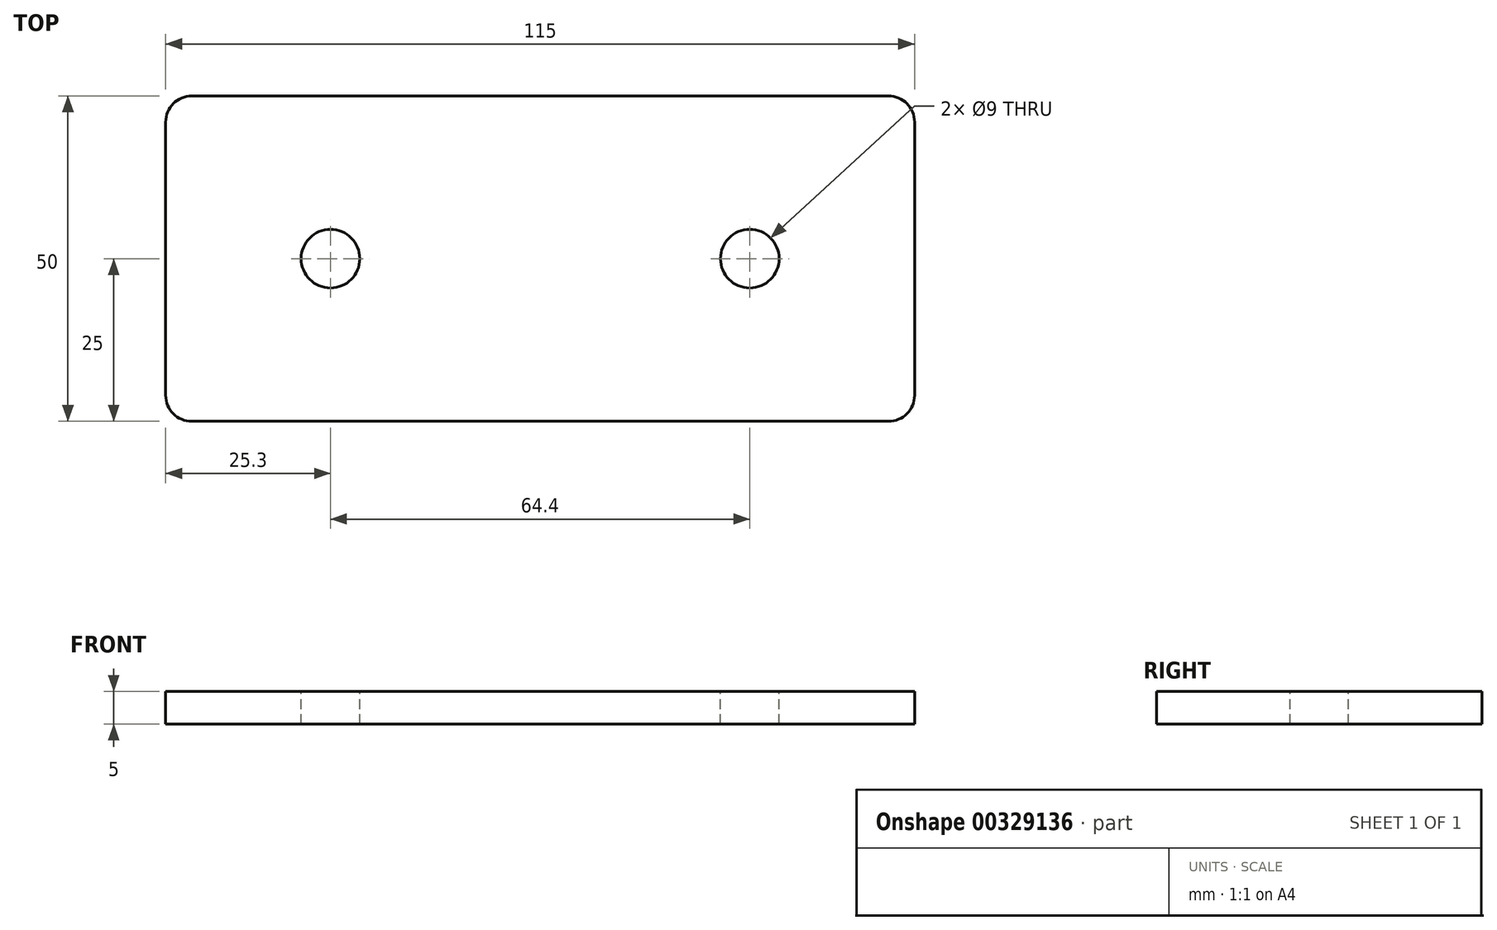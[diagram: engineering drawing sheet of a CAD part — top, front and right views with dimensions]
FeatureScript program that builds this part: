
annotation { "Feature Type Name" : "Feature", "Feature Type Description" : "" }
export const myFeature = defineFeature(function(context is Context, id is Id, definition is map)
    precondition{}
    {
        {
            var Q0;
            Q0=qCreatedBy(makeId("Top.planeOp"),FACE);
            var sketch = newSketch(context, id + "F0", { "sketchPlane" : qUnion([Q0])});
            skLineSegment(sketch, "E0.bottom", {"start": v(0, 0) * mm, "end": v(115, 0) * mm});
            skLineSegment(sketch, "E0.top", {"start": v(0, 50) * mm, "end": v(115, 50) * mm});
            skLineSegment(sketch, "E0.left", {"start": v(0, 0) * mm, "end": v(0, 50) * mm});
            skLineSegment(sketch, "E0.right", {"start": v(115, 0) * mm, "end": v(115, 50) * mm});
            skCircle(sketch, "E1", {"center": v(25.3, 25) * mm, "radius": 4.5 * mm});
            skCircle(sketch, "E2.MirrorC", {"center": v(89.7, 25) * mm, "radius": 4.5 * mm});
            skSolve(sketch);
        }
        {
            var Q0;
            Q0=makeQuery(id+"F0.imprint","IMPRINT",FACE,{"disambiguationData":[TD([[makeQuery(id+"F0.imprint","IMPRINT",EDGE,{"derivedFrom":sQuery(id+"F0.wireOp",EDGE,"E0.bottom")}),1.0]])]});
            extrude(context, id + "F1", {"entities" : qUnion([Q0]), "oppositeDirection" : true, "depth" : 5 * mm});
        }
        {
            var Q0;
            Q0=makeQuery(id+"F1.opExtrude","SWEPT_EDGE",EDGE,{"disambiguationData":[OSD([sQuery(id+"F0.wireOp",EDGE,"E0.bottom"),sQuery(id+"F0.wireOp",EDGE,"E0.right")])]});
            var Q1;
            Q1=makeQuery(id+"F1.opExtrude","SWEPT_EDGE",EDGE,{"disambiguationData":[OSD([sQuery(id+"F0.wireOp",EDGE,"E0.bottom"),sQuery(id+"F0.wireOp",EDGE,"E0.left")])]});
            var Q2;
            Q2=makeQuery(id+"F1.opExtrude","SWEPT_EDGE",EDGE,{"disambiguationData":[OSD([sQuery(id+"F0.wireOp",EDGE,"E0.top"),sQuery(id+"F0.wireOp",EDGE,"E0.right")])]});
            var Q3;
            Q3=makeQuery(id+"F1.opExtrude","SWEPT_EDGE",EDGE,{"disambiguationData":[OSD([sQuery(id+"F0.wireOp",EDGE,"E0.top"),sQuery(id+"F0.wireOp",EDGE,"E0.left")])]});
            fillet(context, id + "F2", {"entities" : qUnion([Q0, Q1, Q2, Q3]), "radius" : 4 * mm, "tangentPropagation" : true, "allowEdgeOverflow" : false});
        }
    });
